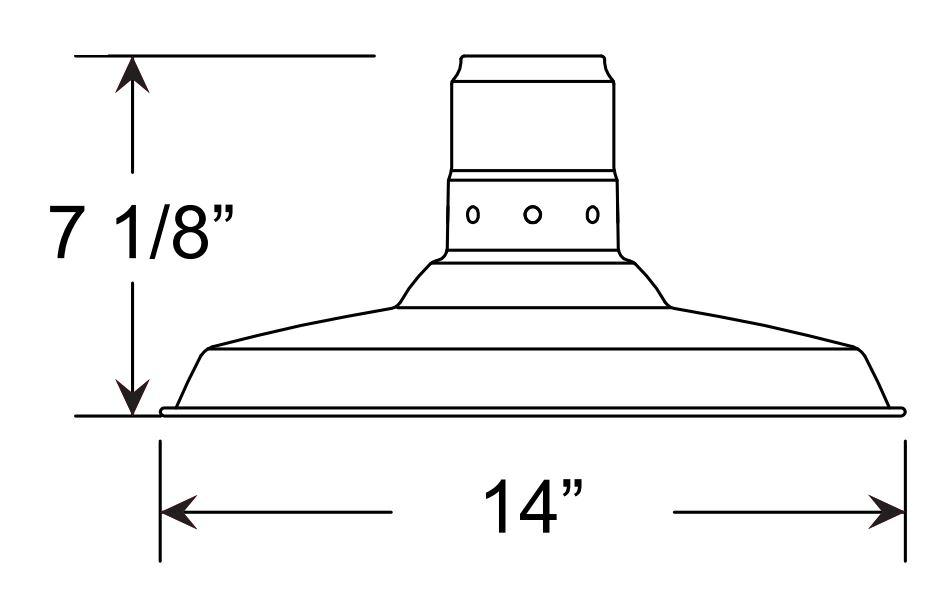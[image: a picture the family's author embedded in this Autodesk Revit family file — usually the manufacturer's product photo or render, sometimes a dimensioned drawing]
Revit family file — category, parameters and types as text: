
# Revit family: BELL(8,10,14) LED
name_source: partatom
category: Lighting Fixtures
units: mm (PartAtom-declared; Revit-internal decimal feet)

## family parameters
Always vertical = Yes
Cut with Voids When Loaded = No
Light Source = Yes
OmniClass Number = 23.80.70.00
OmniClass Title = Lighting
Part Type = Normal
Room Calculation Point = No
Round Connector Dimension = Use Diameter
Shared = No
Work Plane-Based = No

## types (4) — shared parameters
Body Colour = Spun aluminium
Body Material = body
CRI = >90
Color Filter = 16777215
Construction Material = Heavy Duty spun aluminum.
Default Elevation = 0' - 0"
Description = 120-277 Voltage
Dimming = 1%
Dimming Lamp Color Temperature Shift = <None>
Efficiency = 65-125 lumens per watt
Lamp = LED
Life = L70 50,000 hours
Load Classification = Lighting
Manufacturer = ANP Lighting
Power Factor = 1
Tilt Angle = 90.00°
URL = https://www.anplighting.com
Voltage = 277 V
Warranty = 5 year limited warranty

## per-type parameters (varying)
| type | Apparent Load | BELL10 | BELL12 | BELL14 | BELL8 | Fixture Diameter | Fixture Height | Photometric Web File | Wattage Comments | Weight |
| BEL08 | 10 VA | No | No | No | Yes | 0' - 8" | 0' - 6 1/2" | generic.ies | 10W | 2.5 lbs |
| BEL10 | 10 VA | Yes | No | No | No | 0' - 10" | 0' - 7 1/2" | Generic.ies | 10W | 3 lbs |
| BEL12 | 16 VA | No | Yes | No | No | 1' - 0" | 0' - 9" | Generic.ies | 16W | 3.0 lbs |
| BEL14 | 16 VA | No | No | Yes | No | 1' - 2" | 0' - 10 1/2" | generic.ies | 16W | 4.0 lbs |

note: column(s) folded — value = type name in every type: Model

## geometry (parser evidence)
native form markers: Sweep x49
no freeform markers — native parametric forms only
